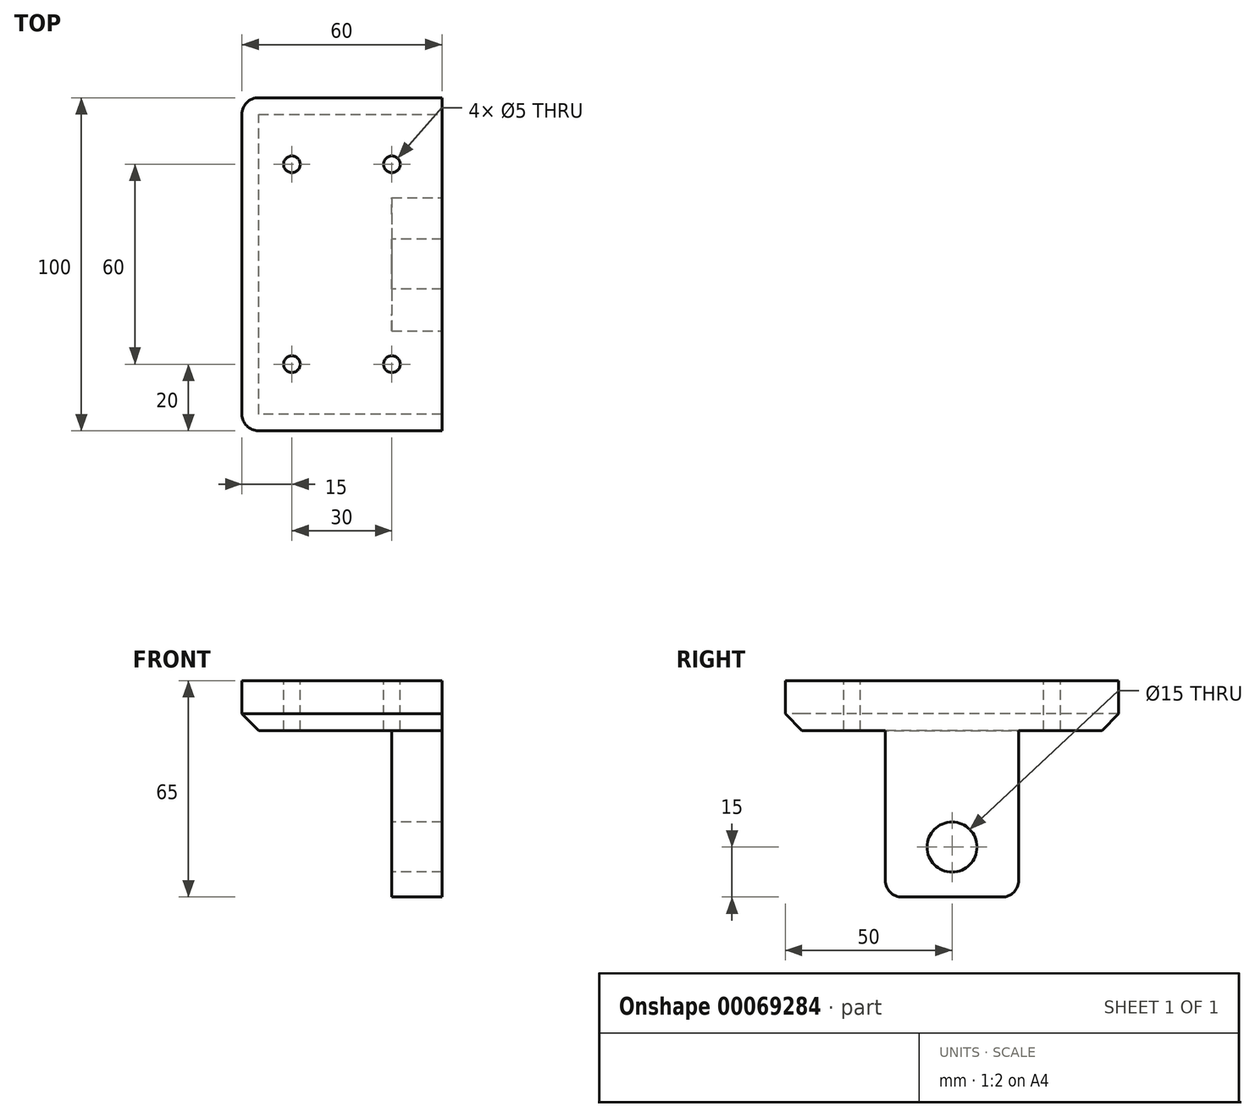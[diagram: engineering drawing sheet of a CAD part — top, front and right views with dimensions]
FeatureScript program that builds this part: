
annotation { "Feature Type Name" : "Feature", "Feature Type Description" : "" }
export const myFeature = defineFeature(function(context is Context, id is Id, definition is map)
    precondition{}
    {
        {
            var Q0;
            Q0=qCreatedBy(makeId("Top.planeOp"),FACE);
            var sketch = newSketch(context, id + "F0", { "sketchPlane" : qUnion([Q0])});
            skLineSegment(sketch, "E0.rect.bottom", {"start": v(-25, 50) * mm, "end": v(30, 50) * mm});
            skLineSegment(sketch, "E0.rect.top", {"start": v(-25, -50) * mm, "end": v(30, -50) * mm});
            skLineSegment(sketch, "E0.rect.left", {"start": v(-30, 45) * mm, "end": v(-30, -45) * mm});
            skLineSegment(sketch, "E0.rect.right", {"start": v(30, 50) * mm, "end": v(30, -50) * mm});
            skPoint(sketch, "E0.rect.middle", {"position": v(0, 0) * mm});
            skPoint(sketch, "E1.visualSharp", {"position": v(-30, 50) * mm});
            skArc(sketch, "E1.filletArc", {"start": v(-25, 50) * mm, "mid": v(-28.54, 48.54) * mm, "end": v(-30, 45) * mm});
            skPoint(sketch, "E2.visualSharp", {"position": v(-30, -50) * mm});
            skArc(sketch, "E2.filletArc", {"start": v(-30, -45) * mm, "mid": v(-28.54, -48.54) * mm, "end": v(-25, -50) * mm});
            skSolve(sketch);
        }
        {
            var Q0;
            Q0 = qSketchRegion(id + "F0", true);
            extrude(context, id + "F1", {"entities" : qUnion([Q0]), "depth" : 15 * mm});
        }
        {
            var Q0;
            Q0=makeQuery(id+"F1.opExtrude","SWEPT_FACE",FACE,{"disambiguationData":[OSD([sQuery(id+"F0.wireOp",EDGE,"E0.rect.right")])]});
            var sketch = newSketch(context, id + "F2", { "sketchPlane" : qUnion([Q0])});
            skLineSegment(sketch, "E3.bottom", {"start": v(20, 0) * mm, "end": v(-20, 0) * mm});
            skLineSegment(sketch, "E3.top", {"start": v(20, -50) * mm, "end": v(-20, -50) * mm});
            skLineSegment(sketch, "E3.left", {"start": v(20, 0) * mm, "end": v(20, -50) * mm});
            skLineSegment(sketch, "E3.right", {"start": v(-20, 0) * mm, "end": v(-20, -50) * mm});
            skSolve(sketch);
        }
        {
            var Q0;
            Q0=makeQuery(id+"F2.imprint","IMPRINT",FACE,{"disambiguationData":[TD([[makeQuery(id+"F2.imprint","IMPRINT",EDGE,{"derivedFrom":sQuery(id+"F2.wireOp",EDGE,"E3.bottom")}),1.0]])]});
            extrude(context, id + "F3", {"entities" : qUnion([Q0]), "oppositeDirection" : true, "depth" : 15 * mm});
        }
        {
            var Q0;
            Q0=makeQuery(id+"F3.opExtrude","SWEPT_BODY",BODY,{"disambiguationData":[OSD([sQuery(id+"F2.wireOp",EDGE,"E3.bottom"),sQuery(id+"F2.wireOp",EDGE,"E3.top"),sQuery(id+"F2.wireOp",EDGE,"E3.left"),sQuery(id+"F2.wireOp",EDGE,"E3.right")])]});
            var Q1;
            Q1=makeQuery(id+"F1.opExtrude","SWEPT_BODY",BODY,{"disambiguationData":[OSD([sQuery(id+"F0.wireOp",EDGE,"E0.rect.bottom"),sQuery(id+"F0.wireOp",EDGE,"E0.rect.top"),sQuery(id+"F0.wireOp",EDGE,"E0.rect.left"),sQuery(id+"F0.wireOp",EDGE,"E0.rect.right"),sQuery(id+"F0.wireOp",EDGE,"E1.filletArc"),sQuery(id+"F0.wireOp",EDGE,"E2.filletArc")])]});
            booleanBodies(context, id + "F4", {"operationType" : BooleanOperationType.UNION, "tools" : qUnion([Q0, Q1])});
        }
        {
            var Q0;
            Q0=makeQuery(id+"F3.opExtrude","CAP_EDGE",EDGE,{"disambiguationData":[OSD([sQuery(id+"F2.wireOp",EDGE,"E3.bottom")])],"isStart":false});
            var Q1;
            Q1=makeQuery(id+"F3.opExtrude","SWEPT_EDGE",EDGE,{"disambiguationData":[OSD([sQuery(id+"F2.wireOp",EDGE,"E3.top"),sQuery(id+"F2.wireOp",EDGE,"E3.left")])]});
            var Q2;
            Q2=makeQuery(id+"F3.opExtrude","SWEPT_EDGE",EDGE,{"disambiguationData":[OSD([sQuery(id+"F2.wireOp",EDGE,"E3.top"),sQuery(id+"F2.wireOp",EDGE,"E3.right")])]});
            var Q3;
            Q3=makeQuery(id+"F3.opExtrude","SWEPT_EDGE",EDGE,{"disambiguationData":[OSD([sQuery(id+"F0.wireOp",EDGE,"E0.rect.right"),sQuery(id+"F2.wireOp",EDGE,"E3.bottom"),sQuery(id+"F2.wireOp",EDGE,"E3.left")])]});
            var Q4;
            Q4=makeQuery(id+"F3.opExtrude","SWEPT_EDGE",EDGE,{"disambiguationData":[OSD([sQuery(id+"F0.wireOp",EDGE,"E0.rect.right"),sQuery(id+"F2.wireOp",EDGE,"E3.bottom"),sQuery(id+"F2.wireOp",EDGE,"E3.right")])]});
            fillet(context, id + "F5", {"entities" : qUnion([Q0, Q1, Q2, Q3, Q4]), "radius" : 5 * mm, "tangentPropagation" : true, "allowEdgeOverflow" : false});
        }
        {
            var Q0;
            Q0=makeQuery(id+"F1.opExtrude","CAP_EDGE",EDGE,{"disambiguationData":[OSD([sQuery(id+"F0.wireOp",EDGE,"E0.rect.left")])],"isStart":true});
            var Q1;
            Q1=makeQuery(id+"F1.opExtrude","CAP_EDGE",EDGE,{"disambiguationData":[OSD([sQuery(id+"F0.wireOp",EDGE,"E0.rect.bottom")])],"isStart":true});
            var Q2;
            Q2=makeQuery(id+"F1.opExtrude","CAP_EDGE",EDGE,{"disambiguationData":[OSD([sQuery(id+"F0.wireOp",EDGE,"E0.rect.top")])],"isStart":true});
            chamfer(context, id + "F6", {"entities" : qUnion([Q0, Q1, Q2]), "width" : 5 * mm, "tangentPropagation" : true});
        }
        {
            var Q0;
            Q0=makeQuery(id+"F3.opExtrude","CAP_FACE",FACE,{"disambiguationData":[OSD([sQuery(id+"F2.wireOp",EDGE,"E3.bottom"),sQuery(id+"F2.wireOp",EDGE,"E3.top"),sQuery(id+"F2.wireOp",EDGE,"E3.left"),sQuery(id+"F2.wireOp",EDGE,"E3.right")])],"isStart":false});
            var sketch = newSketch(context, id + "F7", { "sketchPlane" : qUnion([Q0])});
            skLineSegment(sketch, "E4", {"start": v(0, -50) * mm, "end": v(0, -5) * mm});
            skCircle(sketch, "E5", {"center": v(0, -35) * mm, "radius": 7.5 * mm});
            skSolve(sketch);
        }
        {
            var Q0;
            {var subQ0=sQuery(id+"F7.wireOp",EDGE,"E5");var subQ1=sQuery(id+"F7.wireOp",EDGE,"E4");var subQ2=makeQuery(id+"F7.imprint","INTERSECT",VERTEX,{"disambiguationData":[OD(0.0)],"derivedFrom":[subQ1,subQ0]});Q0=makeQuery(id+"F7.imprint","IMPRINT",FACE,{"disambiguationData":[TD([[makeQuery(id+"F7.imprint","IMPRINT",EDGE,{"disambiguationData":[TD([[subQ2,-1.0]])],"derivedFrom":subQ1}),-1.0]])]});}
            var Q1;
            {var subQ0=sQuery(id+"F7.wireOp",EDGE,"E5");var subQ1=sQuery(id+"F7.wireOp",EDGE,"E4");var subQ2=makeQuery(id+"F7.imprint","INTERSECT",VERTEX,{"disambiguationData":[OD(0.0)],"derivedFrom":[subQ1,subQ0]});Q1=makeQuery(id+"F7.imprint","IMPRINT",FACE,{"disambiguationData":[TD([[makeQuery(id+"F7.imprint","IMPRINT",EDGE,{"disambiguationData":[TD([[subQ2,-1.0]])],"derivedFrom":subQ1}),1.0]])]});}
            extrude(context, id + "F8", {"entities" : qUnion([Q0, Q1]), "operationType" : NewBodyOperationType.REMOVE, "oppositeDirection" : true, "depth" : 25 * mm});
        }
        {
            var Q0;
            Q0=makeQuery(id+"F1.opExtrude","CAP_FACE",FACE,{"disambiguationData":[OSD([sQuery(id+"F0.wireOp",EDGE,"E0.rect.bottom"),sQuery(id+"F0.wireOp",EDGE,"E0.rect.top"),sQuery(id+"F0.wireOp",EDGE,"E0.rect.left"),sQuery(id+"F0.wireOp",EDGE,"E0.rect.right"),sQuery(id+"F0.wireOp",EDGE,"E1.filletArc"),sQuery(id+"F0.wireOp",EDGE,"E2.filletArc")])],"isStart":false});
            var sketch = newSketch(context, id + "F9", { "sketchPlane" : qUnion([Q0])});
            skCircle(sketch, "E6", {"center": v(-15, -30) * mm, "radius": 2.5 * mm});
            skCircle(sketch, "E7.0.1.0", {"center": v(-15, 30) * mm, "radius": 2.5 * mm});
            skCircle(sketch, "E7.1.0.0", {"center": v(15, -30) * mm, "radius": 2.5 * mm});
            skCircle(sketch, "E7.1.1.0", {"center": v(15, 30) * mm, "radius": 2.5 * mm});
            skLineSegment(sketch, "E7.direction1", {"start": v(-15, -30) * mm, "end": v(15, -30) * mm, "construction": true});
            skLineSegment(sketch, "E7.direction2", {"start": v(-15, -30) * mm, "end": v(-15, 30) * mm, "construction": true});
            skSolve(sketch);
        }
        {
            var Q0;
            Q0 = qSketchRegion(id + "F9", true);
            extrude(context, id + "F10", {"entities" : qUnion([Q0]), "operationType" : NewBodyOperationType.REMOVE, "oppositeDirection" : true, "depth" : 25 * mm});
        }
    });
